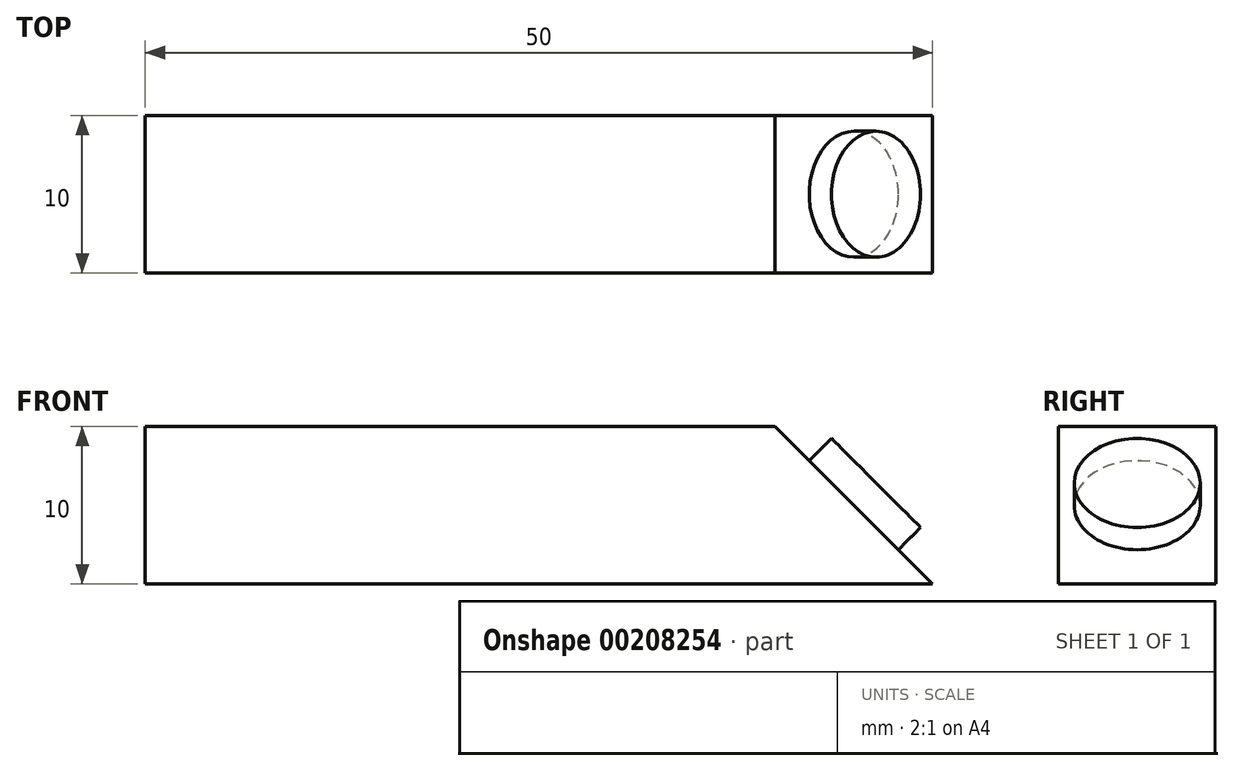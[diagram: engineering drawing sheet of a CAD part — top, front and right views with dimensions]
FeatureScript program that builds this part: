
annotation { "Feature Type Name" : "Feature", "Feature Type Description" : "" }
export const myFeature = defineFeature(function(context is Context, id is Id, definition is map)
    precondition{}
    {
        {
            var Q0;
            Q0=qCreatedBy(makeId("Top.planeOp"),FACE);
            var sketch = newSketch(context, id + "F0", { "sketchPlane" : qUnion([Q0])});
            skLineSegment(sketch, "E0", {"start": v(-46.37, 23.84) * mm, "end": v(3.63, 23.84) * mm});
            skLineSegment(sketch, "E1", {"start": v(3.63, 23.84) * mm, "end": v(3.63, 13.84) * mm});
            skLineSegment(sketch, "E2", {"start": v(3.63, 13.84) * mm, "end": v(-46.37, 13.84) * mm});
            skLineSegment(sketch, "E3", {"start": v(-46.37, 13.84) * mm, "end": v(-46.37, 23.84) * mm});
            skSolve(sketch);
        }
        {
            var Q0;
            Q0=makeQuery(id+"F0.imprint","IMPRINT",FACE,{"disambiguationData":[TD([[makeQuery(id+"F0.imprint","IMPRINT",EDGE,{"derivedFrom":sQuery(id+"F0.wireOp",EDGE,"E0")}),-1.0]])]});
            extrude(context, id + "F1", {"entities" : qUnion([Q0]), "depth" : 10 * mm});
        }
        {
            var Q0;
            Q0=makeQuery(id+"F1.opExtrude","CAP_EDGE",EDGE,{"disambiguationData":[OSD([sQuery(id+"F0.wireOp",EDGE,"E1")])],"isStart":false});
            chamfer(context, id + "F2", {"entities" : qUnion([Q0]), "width" : 10 * mm, "tangentPropagation" : true});
        }
        {
            var Q0;
            Q0=makeQuery(id+"F2.opChamfer","BLEND_FACE",FACE,{"disambiguationData":[OSD([sQuery(id+"F0.wireOp",EDGE,"E1")])]});
            var sketch = newSketch(context, id + "F3", { "sketchPlane" : qUnion([Q0])});
            skCircle(sketch, "E4", {"center": v(18.84, 4.5) * mm, "radius": 4 * mm});
            skSolve(sketch);
        }
        {
            var Q0;
            Q0=makeQuery(id+"F3.imprint","IMPRINT",FACE,{"disambiguationData":[TD([[makeQuery(id+"F3.imprint","IMPRINT",EDGE,{"derivedFrom":sQuery(id+"F3.wireOp",EDGE,"E4")}),1.0]])]});
            extrude(context, id + "F4", {"entities" : qUnion([Q0]), "operationType" : NewBodyOperationType.ADD, "depth" : 2 * mm});
        }
    });
